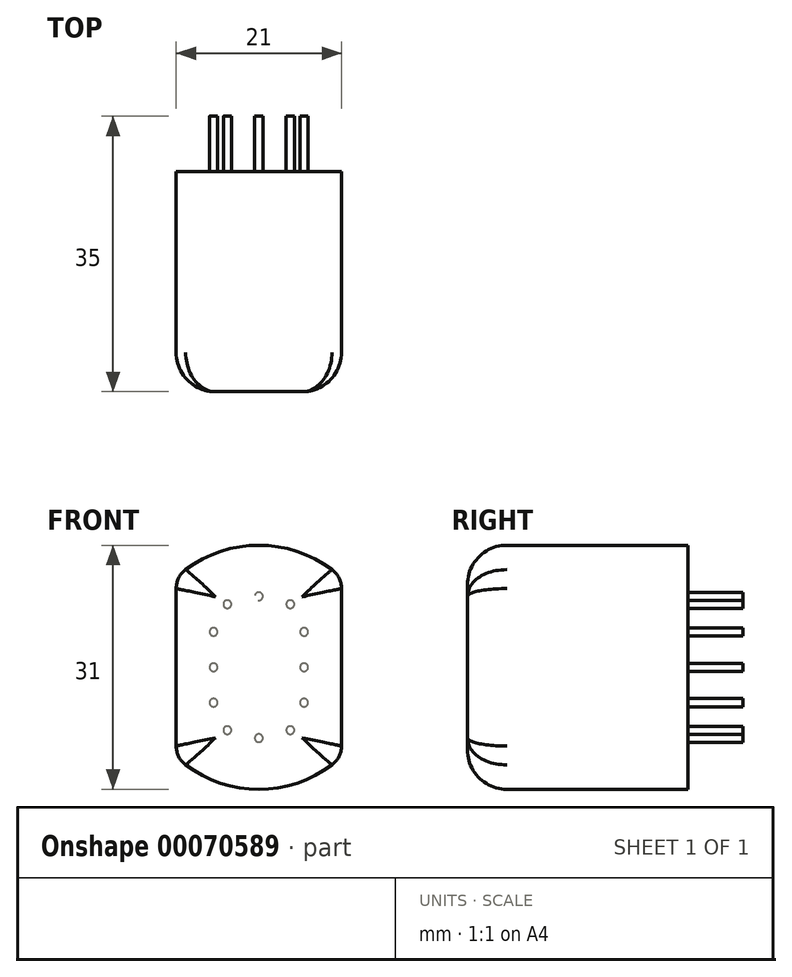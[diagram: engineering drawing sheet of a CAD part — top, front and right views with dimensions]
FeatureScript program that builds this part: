
annotation { "Feature Type Name" : "Feature", "Feature Type Description" : "" }
export const myFeature = defineFeature(function(context is Context, id is Id, definition is map)
    precondition{}
    {
        {
            var Q0;
            Q0=qCreatedBy(makeId("Front.planeOp"),FACE);
            var sketch = newSketch(context, id + "F0", { "sketchPlane" : qUnion([Q0])});
            skLineSegment(sketch, "E0", {"start": v(-10.5, 0) * mm, "end": v(-10.5, 11.4) * mm});
            skLineSegment(sketch, "E1", {"start": v(-10.5, 0) * mm, "end": v(10.5, 0) * mm, "construction": true});
            skLineSegment(sketch, "E2", {"start": v(10.5, 0) * mm, "end": v(10.5, 11.4) * mm});
            skArc(sketch, "E3", {"start": v(10.5, 11.4) * mm, "mid": v(0, 15.5) * mm, "end": v(-10.5, 11.4) * mm});
            skLineSegment(sketch, "E4.MirrorCS", {"start": v(10.5, 0) * mm, "end": v(10.5, -11.4) * mm});
            skArc(sketch, "E5.MirrorCS", {"start": v(10.5, -11.4) * mm, "mid": v(0, -15.5) * mm, "end": v(-10.5, -11.4) * mm});
            skLineSegment(sketch, "E6.MirrorCS", {"start": v(-10.5, 0) * mm, "end": v(-10.5, -11.4) * mm});
            skSolve(sketch);
        }
        {
            var Q0;
            Q0=makeQuery(id+"F0.imprint","IMPRINT",FACE,{"disambiguationData":[TD([[makeQuery(id+"F0.imprint","IMPRINT",EDGE,{"derivedFrom":sQuery(id+"F0.wireOp",EDGE,"E0")}),-1.0]])]});
            extrude(context, id + "F1", {"entities" : qUnion([Q0]), "depth" : 28 * mm});
        }
        {
            var Q0;
            Q0=makeQuery(id+"F1.opExtrude","CAP_FACE",FACE,{"disambiguationData":[OSD([sQuery(id+"F0.wireOp",EDGE,"E0"),sQuery(id+"F0.wireOp",EDGE,"E2"),sQuery(id+"F0.wireOp",EDGE,"E3"),sQuery(id+"F0.wireOp",EDGE,"E4.MirrorCS"),sQuery(id+"F0.wireOp",EDGE,"E5.MirrorCS"),sQuery(id+"F0.wireOp",EDGE,"E6.MirrorCS")])],"isStart":true});
            var sketch = newSketch(context, id + "F2", { "sketchPlane" : qUnion([Q0])});
            skLineSegment(sketch, "E7.rect.bottom", {"start": v(5.75, 4.5) * mm, "end": v(-5.75, 4.5) * mm, "construction": true});
            skLineSegment(sketch, "E7.rect.top", {"start": v(5.75, -4.5) * mm, "end": v(-5.75, -4.5) * mm, "construction": true});
            skLineSegment(sketch, "E7.rect.left", {"start": v(5.75, 4.5) * mm, "end": v(5.75, -4.5) * mm, "construction": true});
            skLineSegment(sketch, "E7.rect.right", {"start": v(-5.75, 4.5) * mm, "end": v(-5.75, -4.5) * mm, "construction": true});
            skPoint(sketch, "E7.rect.middle", {"position": v(0, 0) * mm});
            skLineSegment(sketch, "E8.rect.bottom", {"start": v(4, 8) * mm, "end": v(-4, 8) * mm, "construction": true});
            skLineSegment(sketch, "E8.rect.top", {"start": v(4, -8) * mm, "end": v(-4, -8) * mm, "construction": true});
            skLineSegment(sketch, "E8.rect.left", {"start": v(4, 8) * mm, "end": v(4, -8) * mm, "construction": true});
            skLineSegment(sketch, "E8.rect.right", {"start": v(-4, 8) * mm, "end": v(-4, -8) * mm, "construction": true});
            skLineSegment(sketch, "E9", {"start": v(0, 9) * mm, "end": v(0, -9) * mm, "construction": true});
            skLineSegment(sketch, "E10", {"start": v(-5.75, 0) * mm, "end": v(5.75, 0) * mm, "construction": true});
            skCircle(sketch, "E11", {"center": v(0, 9) * mm, "radius": 0.52 * mm});
            skCircle(sketch, "E12", {"center": v(4, 8) * mm, "radius": 0.52 * mm});
            skCircle(sketch, "E13", {"center": v(5.75, 4.5) * mm, "radius": 0.52 * mm});
            skCircle(sketch, "E14", {"center": v(5.75, 0) * mm, "radius": 0.52 * mm});
            skCircle(sketch, "E15", {"center": v(5.75, -4.5) * mm, "radius": 0.52 * mm});
            skCircle(sketch, "E16", {"center": v(4, -8) * mm, "radius": 0.52 * mm});
            skCircle(sketch, "E17", {"center": v(0, -9) * mm, "radius": 0.52 * mm});
            skCircle(sketch, "E18", {"center": v(-4, -8) * mm, "radius": 0.52 * mm});
            skCircle(sketch, "E19", {"center": v(-5.75, -4.5) * mm, "radius": 0.52 * mm});
            skCircle(sketch, "E20", {"center": v(-5.75, 0) * mm, "radius": 0.52 * mm});
            skCircle(sketch, "E21", {"center": v(-5.75, 4.5) * mm, "radius": 0.52 * mm});
            skCircle(sketch, "E22", {"center": v(-4, 8) * mm, "radius": 0.52 * mm});
            skSolve(sketch);
        }
        {
            var Q0;
            Q0=makeQuery(id+"F2.imprint","IMPRINT",FACE,{"disambiguationData":[TD([[makeQuery(id+"F2.imprint","IMPRINT",EDGE,{"derivedFrom":sQuery(id+"F2.wireOp",EDGE,"E22")}),1.0]])]});
            var Q1;
            Q1=makeQuery(id+"F2.imprint","IMPRINT",FACE,{"disambiguationData":[TD([[makeQuery(id+"F2.imprint","IMPRINT",EDGE,{"derivedFrom":sQuery(id+"F2.wireOp",EDGE,"E11")}),1.0]])]});
            var Q2;
            Q2=makeQuery(id+"F2.imprint","IMPRINT",FACE,{"disambiguationData":[TD([[makeQuery(id+"F2.imprint","IMPRINT",EDGE,{"derivedFrom":sQuery(id+"F2.wireOp",EDGE,"E12")}),1.0]])]});
            var Q3;
            Q3=makeQuery(id+"F2.imprint","IMPRINT",FACE,{"disambiguationData":[TD([[makeQuery(id+"F2.imprint","IMPRINT",EDGE,{"derivedFrom":sQuery(id+"F2.wireOp",EDGE,"E13")}),1.0]])]});
            var Q4;
            Q4=makeQuery(id+"F2.imprint","IMPRINT",FACE,{"disambiguationData":[TD([[makeQuery(id+"F2.imprint","IMPRINT",EDGE,{"derivedFrom":sQuery(id+"F2.wireOp",EDGE,"E14")}),1.0]])]});
            var Q5;
            Q5=makeQuery(id+"F2.imprint","IMPRINT",FACE,{"disambiguationData":[TD([[makeQuery(id+"F2.imprint","IMPRINT",EDGE,{"derivedFrom":sQuery(id+"F2.wireOp",EDGE,"E15")}),1.0]])]});
            var Q6;
            Q6=makeQuery(id+"F2.imprint","IMPRINT",FACE,{"disambiguationData":[TD([[makeQuery(id+"F2.imprint","IMPRINT",EDGE,{"derivedFrom":sQuery(id+"F2.wireOp",EDGE,"E16")}),1.0]])]});
            var Q7;
            Q7=makeQuery(id+"F2.imprint","IMPRINT",FACE,{"disambiguationData":[TD([[makeQuery(id+"F2.imprint","IMPRINT",EDGE,{"derivedFrom":sQuery(id+"F2.wireOp",EDGE,"E17")}),1.0]])]});
            var Q8;
            Q8=makeQuery(id+"F2.imprint","IMPRINT",FACE,{"disambiguationData":[TD([[makeQuery(id+"F2.imprint","IMPRINT",EDGE,{"derivedFrom":sQuery(id+"F2.wireOp",EDGE,"E18")}),1.0]])]});
            var Q9;
            Q9=makeQuery(id+"F2.imprint","IMPRINT",FACE,{"disambiguationData":[TD([[makeQuery(id+"F2.imprint","IMPRINT",EDGE,{"derivedFrom":sQuery(id+"F2.wireOp",EDGE,"E19")}),1.0]])]});
            var Q10;
            Q10=makeQuery(id+"F2.imprint","IMPRINT",FACE,{"disambiguationData":[TD([[makeQuery(id+"F2.imprint","IMPRINT",EDGE,{"derivedFrom":sQuery(id+"F2.wireOp",EDGE,"E20")}),1.0]])]});
            var Q11;
            Q11=makeQuery(id+"F2.imprint","IMPRINT",FACE,{"disambiguationData":[TD([[makeQuery(id+"F2.imprint","IMPRINT",EDGE,{"derivedFrom":sQuery(id+"F2.wireOp",EDGE,"E21")}),1.0]])]});
            extrude(context, id + "F3", {"entities" : qUnion([Q0, Q1, Q2, Q3, Q4, Q5, Q6, Q7, Q8, Q9, Q10, Q11]), "operationType" : NewBodyOperationType.ADD, "depth" : 7 * mm});
        }
        {
            var Q0;
            Q0=makeQuery(id+"F1.opExtrude","CAP_FACE",FACE,{"disambiguationData":[OSD([sQuery(id+"F0.wireOp",EDGE,"E0"),sQuery(id+"F0.wireOp",EDGE,"E2"),sQuery(id+"F0.wireOp",EDGE,"E3"),sQuery(id+"F0.wireOp",EDGE,"E4.MirrorCS"),sQuery(id+"F0.wireOp",EDGE,"E5.MirrorCS"),sQuery(id+"F0.wireOp",EDGE,"E6.MirrorCS")])],"isStart":false});
            fillet(context, id + "F4", {"entities" : qUnion([Q0]), "radius" : 5 * mm, "tangentPropagation" : true, "allowEdgeOverflow" : false});
        }
        {
            var Q0;
            Q0=makeQuery(id+"F4.opFillet","BLEND_EDGE",EDGE,{"blendedFrom":[makeQuery(id+"F1.opExtrude","CAP_EDGE",EDGE,{"disambiguationData":[OSD([sQuery(id+"F0.wireOp",EDGE,"E2"),sQuery(id+"F0.wireOp",EDGE,"E4.MirrorCS")])],"isStart":false}),makeQuery(id+"F1.opExtrude","CAP_EDGE",EDGE,{"disambiguationData":[OSD([sQuery(id+"F0.wireOp",EDGE,"E3")])],"isStart":false})],"blendedInto":[]});
            var Q1;
            Q1=makeQuery(id+"F4.opFillet","BLEND_EDGE",EDGE,{"blendedFrom":[makeQuery(id+"F1.opExtrude","CAP_EDGE",EDGE,{"disambiguationData":[OSD([sQuery(id+"F0.wireOp",EDGE,"E0"),sQuery(id+"F0.wireOp",EDGE,"E6.MirrorCS")])],"isStart":false}),makeQuery(id+"F1.opExtrude","CAP_EDGE",EDGE,{"disambiguationData":[OSD([sQuery(id+"F0.wireOp",EDGE,"E3")])],"isStart":false})],"blendedInto":[]});
            var Q2;
            Q2=makeQuery(id+"F4.opFillet","BLEND_EDGE",EDGE,{"blendedFrom":[makeQuery(id+"F1.opExtrude","CAP_EDGE",EDGE,{"disambiguationData":[OSD([sQuery(id+"F0.wireOp",EDGE,"E0"),sQuery(id+"F0.wireOp",EDGE,"E6.MirrorCS")])],"isStart":false}),makeQuery(id+"F1.opExtrude","CAP_EDGE",EDGE,{"disambiguationData":[OSD([sQuery(id+"F0.wireOp",EDGE,"E5.MirrorCS")])],"isStart":false})],"blendedInto":[]});
            var Q3;
            Q3=makeQuery(id+"F4.opFillet","BLEND_EDGE",EDGE,{"blendedFrom":[makeQuery(id+"F1.opExtrude","CAP_EDGE",EDGE,{"disambiguationData":[OSD([sQuery(id+"F0.wireOp",EDGE,"E2"),sQuery(id+"F0.wireOp",EDGE,"E4.MirrorCS")])],"isStart":false}),makeQuery(id+"F1.opExtrude","CAP_EDGE",EDGE,{"disambiguationData":[OSD([sQuery(id+"F0.wireOp",EDGE,"E5.MirrorCS")])],"isStart":false})],"blendedInto":[]});
            fillet(context, id + "F5", {"entities" : qUnion([Q0, Q1, Q2, Q3]), "radius" : 3 * mm, "tangentPropagation" : true, "allowEdgeOverflow" : false});
        }
    });
